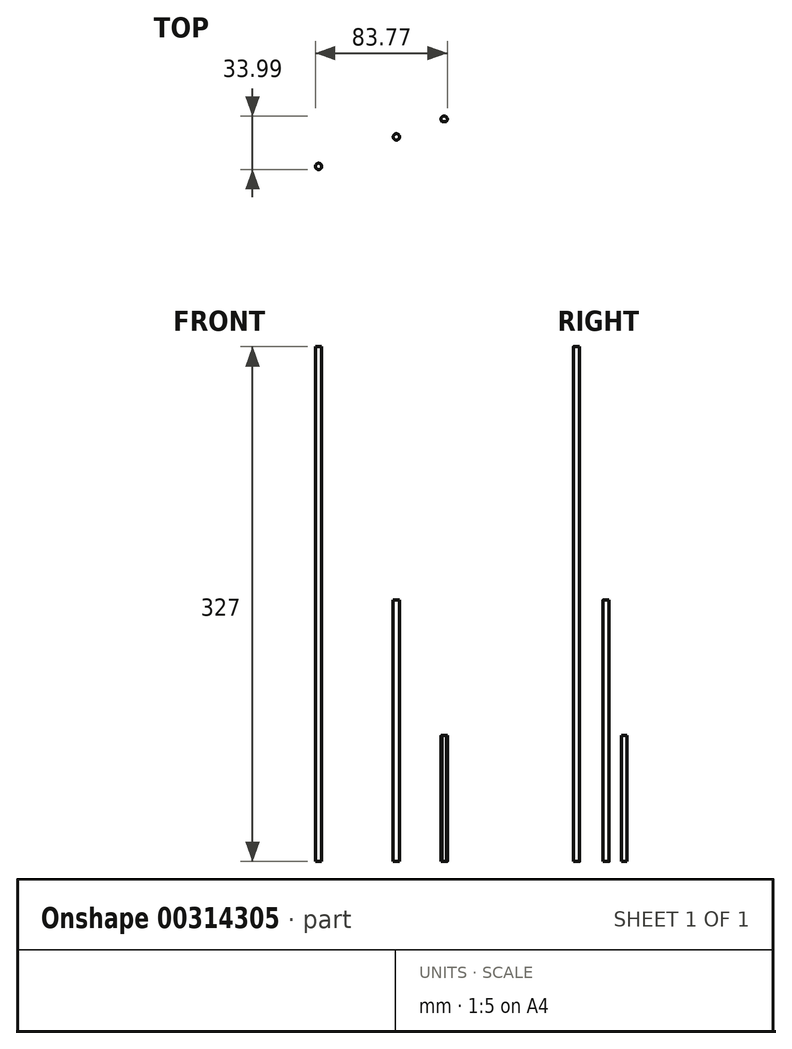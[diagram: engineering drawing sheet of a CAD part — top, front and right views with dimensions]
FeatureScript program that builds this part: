
annotation { "Feature Type Name" : "Feature", "Feature Type Description" : "" }
export const myFeature = defineFeature(function(context is Context, id is Id, definition is map)
    precondition{}
    {
        {
            var Q0;
            Q0=qCreatedBy(makeId("Top.planeOp"),FACE);
            var sketch = newSketch(context, id + "F0", { "sketchPlane" : qUnion([Q0]), "asVersion" : FeatureScriptVersionNumber.V442_PARTING_OUT_TARGET_READONLY});
            skArc(sketch, "E0", {"start": v(1.32, -1.5) * mm, "mid": v(0, 2) * mm, "end": v(-1.32, -1.5) * mm});
            skLineSegment(sketch, "E1", {"start": v(-1.32, -1.5) * mm, "end": v(1.32, -1.5) * mm});
            skCircle(sketch, "E2", {"center": v(-30.35, -11.24) * mm, "radius": 2 * mm});
            skCircle(sketch, "E3", {"center": v(-79.77, -30) * mm, "radius": 2 * mm});
            skSolve(sketch);
        }
        {
            var Q0;
            Q0=makeQuery(id+"F0.imprint","IMPRINT",FACE,{"disambiguationData":[TD([[makeQuery(id+"F0.imprint","IMPRINT",EDGE,{"derivedFrom":sQuery(id+"F0.wireOp",EDGE,"E0")}),1.0]])]});
            extrude(context, id + "F1", {"entities" : qUnion([Q0]), "depth" : 80 * mm});
        }
        {
            var Q0;
            Q0=makeQuery(id+"F0.imprint","IMPRINT",FACE,{"disambiguationData":[TD([[makeQuery(id+"F0.imprint","IMPRINT",EDGE,{"derivedFrom":sQuery(id+"F0.wireOp",EDGE,"E2")}),1.0]])]});
            extrude(context, id + "F2", {"entities" : qUnion([Q0]), "depth" : 166 * mm});
        }
        {
            var Q0;
            Q0=makeQuery(id+"F0.imprint","IMPRINT",FACE,{"disambiguationData":[TD([[makeQuery(id+"F0.imprint","IMPRINT",EDGE,{"derivedFrom":sQuery(id+"F0.wireOp",EDGE,"E3")}),1.0]])]});
            extrude(context, id + "F3", {"entities" : qUnion([Q0]), "depth" : 327 * mm});
        }
    });
